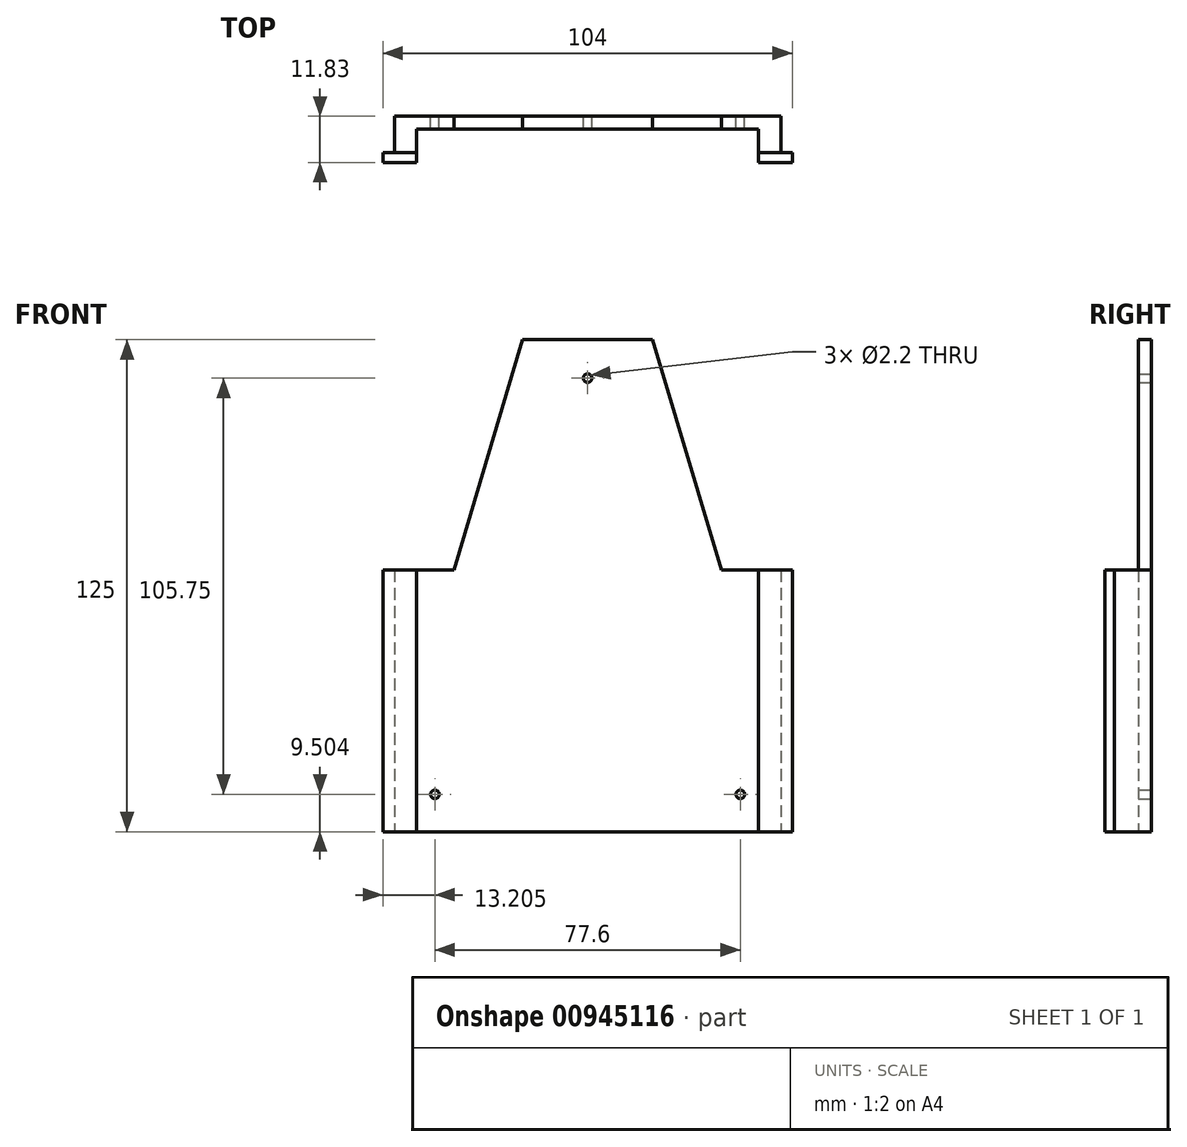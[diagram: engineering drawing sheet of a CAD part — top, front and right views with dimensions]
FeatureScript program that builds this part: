
annotation { "Feature Type Name" : "Feature", "Feature Type Description" : "" }
export const myFeature = defineFeature(function(context is Context, id is Id, definition is map)
    precondition{}
    {
        {
            var Q0;
            Q0=qCreatedBy(makeId("Front.planeOp"),FACE);
            var sketch = newSketch(context, id + "F0", { "sketchPlane" : qUnion([Q0])});
            skLineSegment(sketch, "E0.bottom", {"start": v(-25.95, 14.83) * mm, "end": v(78.05, 14.83) * mm});
            skLineSegment(sketch, "E0.top", {"start": v(-25.95, -51.67) * mm, "end": v(78.05, -51.67) * mm});
            skLineSegment(sketch, "E0.left", {"start": v(-25.95, 14.83) * mm, "end": v(-25.95, -51.67) * mm});
            skLineSegment(sketch, "E0.right", {"start": v(78.05, 14.83) * mm, "end": v(78.05, -51.67) * mm});
            skLineSegment(sketch, "E1", {"start": v(-25.95, 14.83) * mm, "end": v(-23.04, 14.83) * mm});
            skLineSegment(sketch, "E2", {"start": v(-23.04, 14.83) * mm, "end": v(-23.04, -51.67) * mm});
            skLineSegment(sketch, "E3", {"start": v(26.05, 14.83) * mm, "end": v(26.05, -51.67) * mm});
            skLineSegment(sketch, "E4", {"start": v(26.05, 14.83) * mm, "end": v(-17.35, 14.83) * mm});
            skLineSegment(sketch, "E5", {"start": v(-17.35, 14.83) * mm, "end": v(-17.35, -51.67) * mm});
            skLineSegment(sketch, "E6", {"start": v(-17.35, 14.83) * mm, "end": v(-20.85, 14.83) * mm});
            skLineSegment(sketch, "E7.MirrorCS", {"start": v(69.45, 14.83) * mm, "end": v(69.45, -51.67) * mm});
            skLineSegment(sketch, "E8.MirrorCS", {"start": v(69.45, 14.83) * mm, "end": v(72.95, 14.83) * mm});
            skLineSegment(sketch, "E9.MirrorCS", {"start": v(75.15, 14.83) * mm, "end": v(75.15, -51.67) * mm});
            skSolve(sketch);
        }
        {
            var Q0;
            {var subQ0=sQuery(id+"F0.wireOp",EDGE,"E0.left");Q0=makeQuery(id+"F0.imprint","IMPRINT",FACE,{"disambiguationData":[TD([[makeQuery(id+"F0.imprint","IMPRINT",EDGE,{"derivedFrom":subQ0}),1.0]])]});}
            var Q1;
            {var subQ0=sQuery(id+"F0.wireOp",EDGE,"E0.right");Q1=makeQuery(id+"F0.imprint","IMPRINT",FACE,{"disambiguationData":[TD([[makeQuery(id+"F0.imprint","IMPRINT",EDGE,{"derivedFrom":subQ0}),-1.0]])]});}
            var Q2;
            {var subQ4=sQuery(id+"F0.wireOp",EDGE,"E2");Q2=makeQuery(id+"F0.imprint","IMPRINT",FACE,{"disambiguationData":[TD([[makeQuery(id+"F0.imprint","IMPRINT",EDGE,{"derivedFrom":subQ4}),1.0]])]});}
            var Q3;
            {var subQ0=sQuery(id+"F0.wireOp",EDGE,"1d232c16-9bde-4001-9b06-475ff8e0552f0.MirrorCS");Q3=makeQuery(id+"F0.imprint","IMPRINT",FACE,{"disambiguationData":[TD([[makeQuery(id+"F0.imprint","IMPRINT",EDGE,{"derivedFrom":subQ0}),1.0]])]});}
            var Q4;
            {var subQ1=sQuery(id+"F0.wireOp",EDGE,"E7.MirrorCS");Q4=makeQuery(id+"F0.imprint","IMPRINT",FACE,{"disambiguationData":[TD([[makeQuery(id+"F0.imprint","IMPRINT",EDGE,{"derivedFrom":subQ1}),1.0]])]});}
            extrude(context, id + "F1", {"entities" : qUnion([Q0, Q1, Q2, Q3, Q4]), "depth" : 2.5 * mm, "offsetDistance" : 25 * mm});
        }
        {
            var Q0;
            {var subQ1=sQuery(id+"F0.wireOp",EDGE,"E7.MirrorCS");Q0=makeQuery(id+"F0.imprint","IMPRINT",FACE,{"disambiguationData":[TD([[makeQuery(id+"F0.imprint","IMPRINT",EDGE,{"derivedFrom":subQ1}),1.0]])]});}
            var Q1;
            {var subQ1=sQuery(id+"F0.wireOp",EDGE,"E2");Q1=makeQuery(id+"F0.imprint","IMPRINT",FACE,{"disambiguationData":[TD([[makeQuery(id+"F0.imprint","IMPRINT",EDGE,{"derivedFrom":subQ1}),1.0]])]});}
            extrude(context, id + "F2", {"entities" : qUnion([Q0, Q1]), "oppositeDirection" : true, "depth" : 9.33 * mm, "offsetDistance" : 25 * mm});
        }
        {
            var Q0;
            Q0=makeQuery(id+"F2.opExtrude","CAP_FACE",FACE,{"disambiguationData":[OSD([sQuery(id+"F0.wireOp",EDGE,"E0.bottom"),sQuery(id+"F0.wireOp",EDGE,"E0.top"),sQuery(id+"F0.wireOp",EDGE,"E2"),sQuery(id+"F0.wireOp",EDGE,"E5"),sQuery(id+"F0.wireOp",EDGE,"IQfkofzU-REa2-stQb-JhD2-gqWbtNb49Qhc"),sQuery(id+"F0.wireOp",EDGE,"y712Ytxc-mr80-ixlf-w5sj-AXbWPCbkoOpe")])],"isStart":false});
            var sketch = newSketch(context, id + "F3", { "sketchPlane" : qUnion([Q0])});
            skLineSegment(sketch, "E10.left", {"start": v(23.04, 14.83) * mm, "end": v(23.04, -51.67) * mm});
            skLineSegment(sketch, "E11", {"start": v(23.04, 14.83) * mm, "end": v(-75.15, 14.83) * mm});
            skLineSegment(sketch, "E12", {"start": v(-75.15, 14.83) * mm, "end": v(-75.15, -51.67) * mm});
            skLineSegment(sketch, "E13", {"start": v(-75.15, -51.67) * mm, "end": v(23.04, -51.67) * mm});
            skLineSegment(sketch, "E14", {"start": v(-26.05, -51.67) * mm, "end": v(-26.05, 73.33) * mm, "construction": true});
            skLineSegment(sketch, "E15", {"start": v(-26.05, 73.33) * mm, "end": v(-42.55, 73.33) * mm});
            skLineSegment(sketch, "E16", {"start": v(-26.05, 14.83) * mm, "end": v(-60.05, 14.83) * mm});
            skLineSegment(sketch, "E17", {"start": v(-60.05, 14.83) * mm, "end": v(-42.55, 73.33) * mm});
            skLineSegment(sketch, "E18.MirrorCS", {"start": v(7.95, 14.83) * mm, "end": v(-9.55, 73.33) * mm});
            skLineSegment(sketch, "E19.MirrorCS", {"start": v(-26.05, 73.33) * mm, "end": v(-9.55, 73.33) * mm});
            skCircle(sketch, "E20", {"center": v(-64.85, -42.17) * mm, "radius": 1.1 * mm});
            skCircle(sketch, "E21.MirrorC", {"center": v(12.75, -42.17) * mm, "radius": 1.1 * mm});
            skCircle(sketch, "E22", {"center": v(-26.05, 63.58) * mm, "radius": 1.1 * mm});
            skSolve(sketch);
        }
        {
            var Q0;
            {var subQ5=makeQuery(id+"F2.opExtrude","CAP_EDGE",EDGE,{"disambiguationData":[OSD([sQuery(id+"F0.wireOp",EDGE,"E5")])],"isStart":false});Q0=makeQuery(id+"F3.imprint","IMPRINT",FACE,{"disambiguationData":[TD([[makeQuery(id+"F3.imprint","IMPRINT",EDGE,{"derivedFrom":subQ5}),-1.0]])]});}
            var Q1;
            {var subQ3=sQuery(id+"F3.wireOp",EDGE,"E18.MirrorCS");Q1=makeQuery(id+"F3.imprint","IMPRINT",FACE,{"disambiguationData":[TD([[makeQuery(id+"F3.imprint","IMPRINT",EDGE,{"derivedFrom":subQ3}),1.0]])]});}
            var Q2;
            {var subQ0=sQuery(id+"F3.wireOp",EDGE,"E15");Q2=makeQuery(id+"F3.imprint","IMPRINT",FACE,{"disambiguationData":[TD([[makeQuery(id+"F3.imprint","IMPRINT",EDGE,{"derivedFrom":subQ0}),1.0]])]});}
            var Q3;
            {var subQ1=sQuery(id+"F3.wireOp",EDGE,"E12");Q3=makeQuery(id+"F3.imprint","IMPRINT",FACE,{"disambiguationData":[TD([[makeQuery(id+"F3.imprint","IMPRINT",EDGE,{"derivedFrom":subQ1}),1.0]])]});}
            extrude(context, id + "F4", {"entities" : qUnion([Q0, Q1, Q2, Q3]), "operationType" : NewBodyOperationType.ADD, "oppositeDirection" : true, "depth" : 3.25 * mm, "offsetDistance" : 25 * mm});
        }
    });
